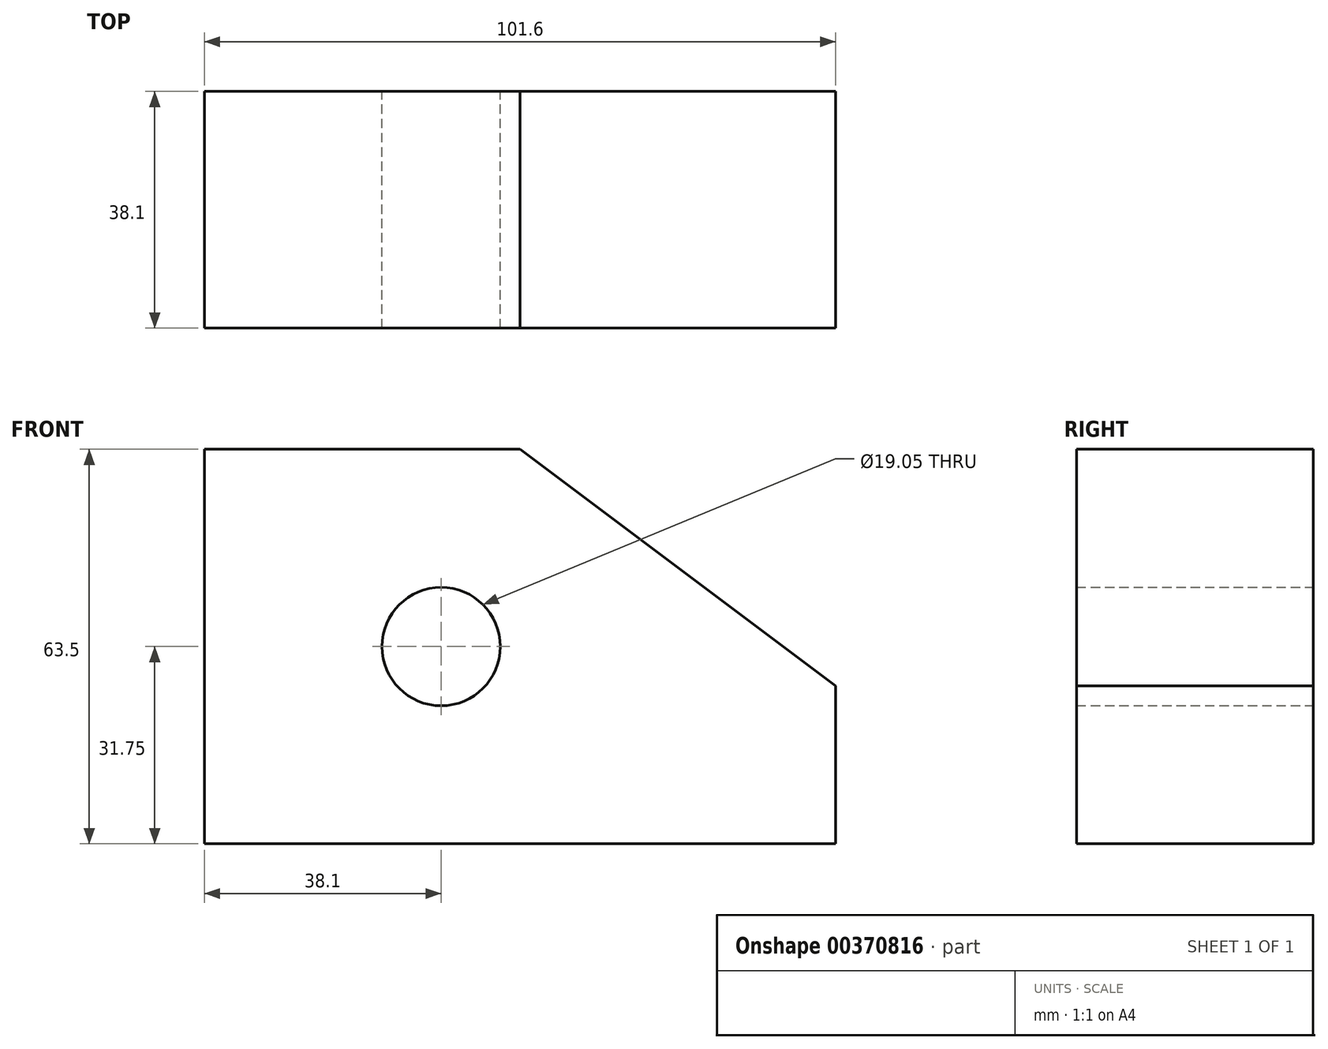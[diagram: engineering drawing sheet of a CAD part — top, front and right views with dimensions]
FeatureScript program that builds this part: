
annotation { "Feature Type Name" : "Feature", "Feature Type Description" : "" }
export const myFeature = defineFeature(function(context is Context, id is Id, definition is map)
    precondition{}
    {
        {
            var Q0;
            Q0=qCreatedBy(makeId("Front.planeOp"),FACE);
            var sketch = newSketch(context, id + "F0", { "sketchPlane" : qUnion([Q0])});
            skLineSegment(sketch, "E0", {"start": v(0, 0) * mm, "end": v(0, -63.5) * mm});
            skLineSegment(sketch, "E1", {"start": v(0, 0) * mm, "end": v(50.8, 0) * mm});
            skLineSegment(sketch, "E2", {"start": v(0, -63.5) * mm, "end": v(101.6, -63.5) * mm});
            skLineSegment(sketch, "E3", {"start": v(101.6, -63.5) * mm, "end": v(101.6, -38.1) * mm});
            skLineSegment(sketch, "E4", {"start": v(50.8, 0) * mm, "end": v(101.6, -38.1) * mm});
            skCircle(sketch, "E5", {"center": v(38.1, -31.75) * mm, "radius": 9.53 * mm});
            skSolve(sketch);
        }
        {
            var Q0;
            Q0=makeQuery(id+"F0.imprint","IMPRINT",FACE,{"disambiguationData":[TD([[makeQuery(id+"F0.imprint","IMPRINT",EDGE,{"derivedFrom":sQuery(id+"F0.wireOp",EDGE,"E0")}),1.0]])]});
            extrude(context, id + "F1", {"entities" : qUnion([Q0]), "depth" : 38.1 * mm});
        }
    });
